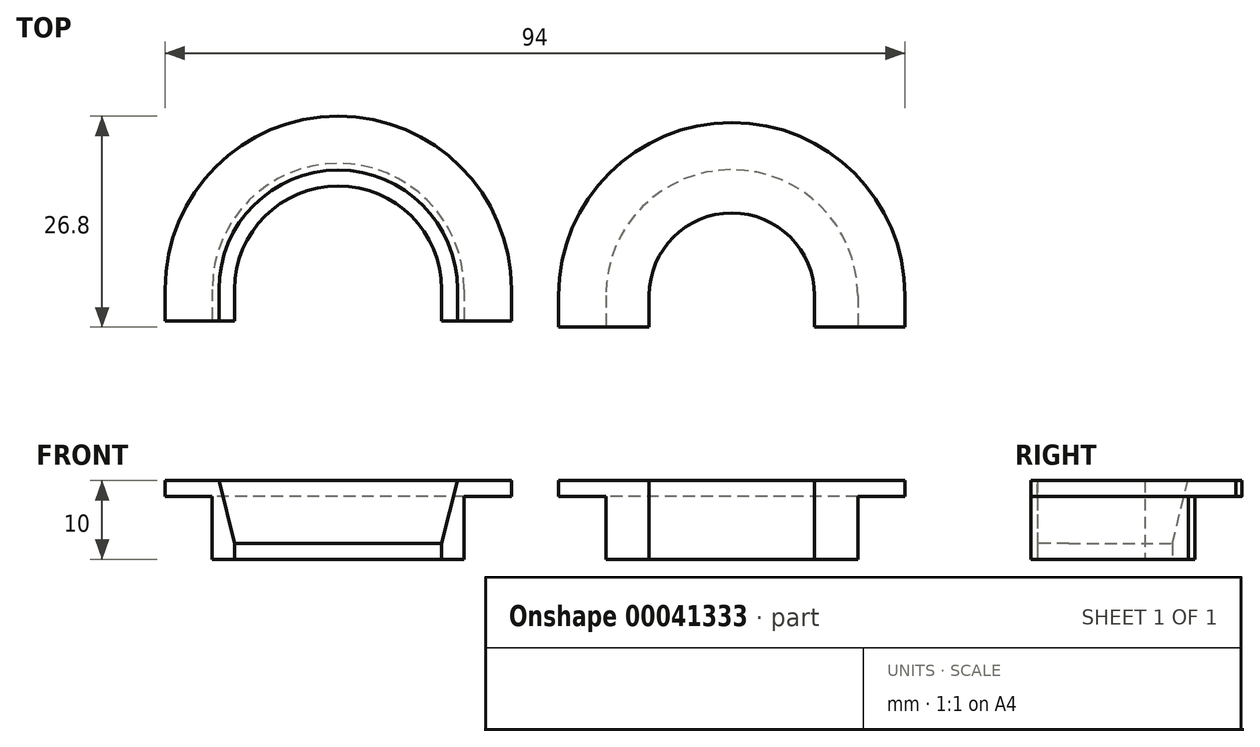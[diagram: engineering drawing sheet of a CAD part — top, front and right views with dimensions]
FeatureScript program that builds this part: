
annotation { "Feature Type Name" : "Feature", "Feature Type Description" : "" }
export const myFeature = defineFeature(function(context is Context, id is Id, definition is map)
    precondition{}
    {
        {
            var Q0;
            Q0=qCreatedBy(makeId("Top.planeOp"),FACE);
            var sketch = newSketch(context, id + "F0", { "sketchPlane" : qUnion([Q0])});
            skArc(sketch, "E0", {"start": v(-8.97, 12.12) * mm, "mid": v(-22.12, 25.27) * mm, "end": v(-35.27, 12.12) * mm});
            skArc(sketch, "E1", {"start": v(-6.12, 12.12) * mm, "mid": v(-22.12, 28.12) * mm, "end": v(-38.12, 12.12) * mm});
            skArc(sketch, "E2", {"start": v(38.38, 11.32) * mm, "mid": v(27.88, 21.82) * mm, "end": v(17.38, 11.32) * mm});
            skArc(sketch, "E3", {"start": v(43.88, 11.32) * mm, "mid": v(27.88, 27.32) * mm, "end": v(11.88, 11.32) * mm});
            skLineSegment(sketch, "E4.top", {"start": v(11.88, 7.32) * mm, "end": v(17.38, 7.32) * mm});
            skLineSegment(sketch, "E4.left", {"start": v(11.88, 11.32) * mm, "end": v(11.88, 7.32) * mm});
            skLineSegment(sketch, "E4.right", {"start": v(17.38, 11.32) * mm, "end": v(17.38, 7.32) * mm});
            skLineSegment(sketch, "E5.top", {"start": v(38.38, 7.32) * mm, "end": v(43.88, 7.32) * mm});
            skLineSegment(sketch, "E5.left", {"start": v(38.38, 11.32) * mm, "end": v(38.38, 7.32) * mm});
            skLineSegment(sketch, "E5.right", {"start": v(43.88, 11.32) * mm, "end": v(43.88, 7.32) * mm});
            skLineSegment(sketch, "E6.top", {"start": v(-8.97, 8.12) * mm, "end": v(-6.12, 8.12) * mm});
            skLineSegment(sketch, "E6.left", {"start": v(-8.97, 12.12) * mm, "end": v(-8.97, 8.12) * mm});
            skLineSegment(sketch, "E6.right", {"start": v(-6.12, 12.12) * mm, "end": v(-6.12, 8.12) * mm});
            skLineSegment(sketch, "E7.top", {"start": v(-38.12, 8.12) * mm, "end": v(-35.27, 8.12) * mm});
            skLineSegment(sketch, "E7.left", {"start": v(-38.12, 12.12) * mm, "end": v(-38.12, 8.12) * mm});
            skLineSegment(sketch, "E7.right", {"start": v(-35.27, 12.12) * mm, "end": v(-35.27, 8.12) * mm});
            skSolve(sketch);
        }
        {
            var Q0;
            Q0=makeQuery(id+"F0.imprint","IMPRINT",FACE,{"disambiguationData":[TD([[makeQuery(id+"F0.imprint","IMPRINT",EDGE,{"derivedFrom":sQuery(id+"F0.wireOp",EDGE,"E0")}),-1.0]])]});
            extrude(context, id + "F1", {"entities" : qUnion([Q0]), "depth" : 10 * mm});
        }
        {
            var Q0;
            Q0=makeQuery(id+"F0.imprint","IMPRINT",FACE,{"disambiguationData":[TD([[makeQuery(id+"F0.imprint","IMPRINT",EDGE,{"derivedFrom":sQuery(id+"F0.wireOp",EDGE,"E2")}),-1.0]])]});
            extrude(context, id + "F2", {"entities" : qUnion([Q0]), "depth" : 8 * mm});
        }
        {
            var Q0;
            Q0=makeQuery(id+"F2.opExtrude","CAP_FACE",FACE,{"disambiguationData":[OSD([sQuery(id+"F0.wireOp",EDGE,"E2"),sQuery(id+"F0.wireOp",EDGE,"E3"),sQuery(id+"F0.wireOp",EDGE,"E4.top"),sQuery(id+"F0.wireOp",EDGE,"E4.left"),sQuery(id+"F0.wireOp",EDGE,"E4.right"),sQuery(id+"F0.wireOp",EDGE,"E5.top"),sQuery(id+"F0.wireOp",EDGE,"E5.left"),sQuery(id+"F0.wireOp",EDGE,"E5.right")])],"isStart":false});
            var sketch = newSketch(context, id + "F3", { "sketchPlane" : qUnion([Q0])});
            skLineSegment(sketch, "E8.0", {"start": v(5.88, 11.32) * mm, "end": v(5.88, 7.32) * mm});
            skArc(sketch, "E8.1", {"start": v(49.88, 11.32) * mm, "mid": v(27.88, 33.32) * mm, "end": v(5.88, 11.32) * mm});
            skLineSegment(sketch, "E8.2", {"start": v(49.88, 11.32) * mm, "end": v(49.88, 7.32) * mm});
            skLineSegment(sketch, "E9", {"start": v(5.88, 7.32) * mm, "end": v(11.88, 7.32) * mm});
            skLineSegment(sketch, "E10", {"start": v(43.88, 7.32) * mm, "end": v(49.88, 7.32) * mm});
            skSolve(sketch);
        }
        {
            var Q0;
            Q0=makeQuery(id+"F3.imprint","IMPRINT",FACE,{"disambiguationData":[TD([[makeQuery(id+"F3.imprint","IMPRINT",EDGE,{"derivedFrom":sQuery(id+"F3.wireOp",EDGE,"E8.0")}),1.0]])]});
            var Q1;
            Q1=makeQuery(id+"F3.imprint","IMPRINT",FACE,{"disambiguationData":[TD([[makeQuery(id+"F3.imprint","IMPRINT",EDGE,{"derivedFrom":makeQuery(id+"F2.opExtrude","CAP_EDGE",EDGE,{"disambiguationData":[OSD([sQuery(id+"F0.wireOp",EDGE,"E2")])],"isStart":false})}),-1.0]])]});
            var Q2;
            Q2=makeQuery(id+"F3.imprint","IMPRINT",FACE,{"disambiguationData":[TD([[makeQuery(id+"F3.imprint","IMPRINT",EDGE,{"derivedFrom":makeQuery(id+"F2.opExtrude","CAP_EDGE",EDGE,{"disambiguationData":[OSD([sQuery(id+"F0.wireOp",EDGE,"E2")])],"isStart":false})}),-1.0]])]});
            extrude(context, id + "F4", {"entities" : qUnion([Q0, Q1, Q2]), "operationType" : NewBodyOperationType.ADD, "depth" : 2 * mm});
        }
        {
            var Q0;
            Q0=makeQuery(id+"F1.opExtrude","CAP_EDGE",EDGE,{"disambiguationData":[OSD([sQuery(id+"F0.wireOp",EDGE,"E0")])],"isStart":false});
            chamfer(context, id + "F5", {"entities" : qUnion([Q0]), "chamferType" : ChamferType.TWO_OFFSETS, "width1" : 8 * mm, "oppositeDirection" : false, "width2" : 2 * mm, "tangentPropagation" : true});
        }
        {
            var Q0;
            Q0=makeQuery(id+"F1.opExtrude","CAP_FACE",FACE,{"disambiguationData":[OSD([sQuery(id+"F0.wireOp",EDGE,"E0"),sQuery(id+"F0.wireOp",EDGE,"E1"),sQuery(id+"F0.wireOp",EDGE,"E6.top"),sQuery(id+"F0.wireOp",EDGE,"E6.left"),sQuery(id+"F0.wireOp",EDGE,"E6.right"),sQuery(id+"F0.wireOp",EDGE,"E7.top"),sQuery(id+"F0.wireOp",EDGE,"E7.left"),sQuery(id+"F0.wireOp",EDGE,"E7.right")])],"isStart":false});
            var sketch = newSketch(context, id + "F6", { "sketchPlane" : qUnion([Q0])});
            skLineSegment(sketch, "E11.0", {"start": v(-44.12, 12.12) * mm, "end": v(-44.12, 8.12) * mm});
            skArc(sketch, "E11.1", {"start": v(-0.12, 12.12) * mm, "mid": v(-22.12, 34.12) * mm, "end": v(-44.12, 12.12) * mm});
            skLineSegment(sketch, "E11.2", {"start": v(-0.12, 12.12) * mm, "end": v(-0.12, 8.12) * mm});
            skLineSegment(sketch, "E12", {"start": v(-44.12, 8.12) * mm, "end": v(-38.12, 8.12) * mm});
            skLineSegment(sketch, "E13", {"start": v(-6.12, 8.12) * mm, "end": v(-0.12, 8.12) * mm});
            skSolve(sketch);
        }
        {
            var Q0;
            Q0=makeQuery(id+"F6.imprint","IMPRINT",FACE,{"disambiguationData":[TD([[makeQuery(id+"F6.imprint","IMPRINT",EDGE,{"derivedFrom":sQuery(id+"F6.wireOp",EDGE,"E11.0")}),1.0]])]});
            extrude(context, id + "F7", {"entities" : qUnion([Q0]), "operationType" : NewBodyOperationType.ADD, "oppositeDirection" : true, "depth" : 2 * mm});
        }
    });
